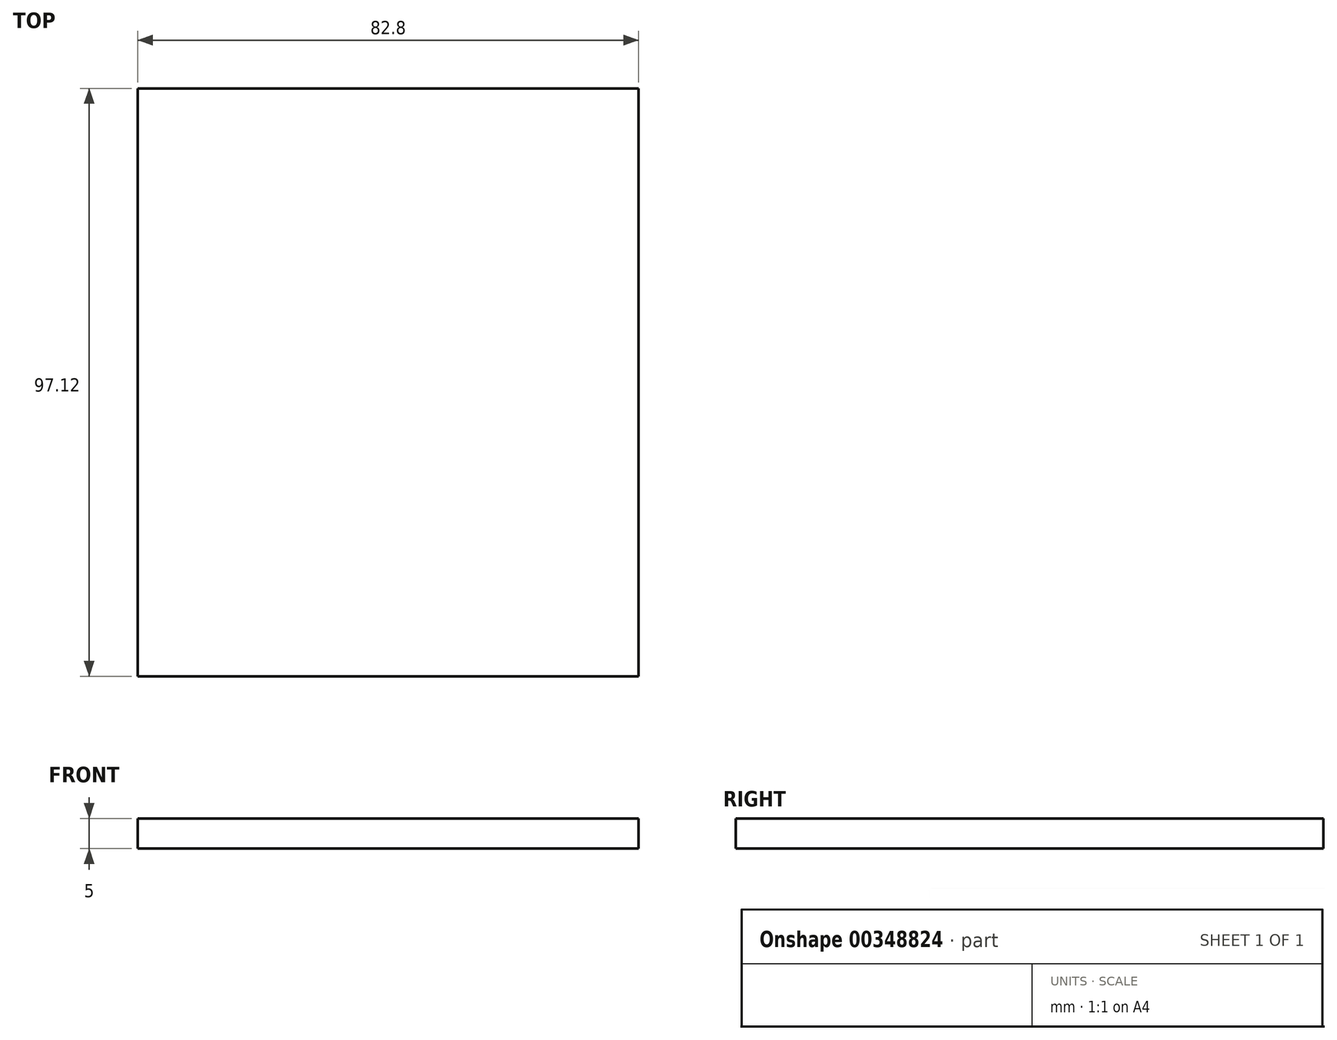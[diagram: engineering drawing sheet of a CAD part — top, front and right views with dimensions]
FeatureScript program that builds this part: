
annotation { "Feature Type Name" : "Feature", "Feature Type Description" : "" }
export const myFeature = defineFeature(function(context is Context, id is Id, definition is map)
    precondition{}
    {
        {
            var Q0;
            Q0=qCreatedBy(makeId("Top.planeOp"),FACE);
            var sketch = newSketch(context, id + "F0", { "sketchPlane" : qUnion([Q0])});
            skLineSegment(sketch, "E0.bottom", {"start": v(-41.4, 48.56) * mm, "end": v(41.4, 48.56) * mm});
            skLineSegment(sketch, "E0.left", {"start": v(-41.4, 48.56) * mm, "end": v(-41.4, -48.56) * mm});
            skLineSegment(sketch, "E0.right", {"start": v(41.4, 48.56) * mm, "end": v(41.4, -48.56) * mm});
            skLineSegment(sketch, "E1", {"start": v(-41.4, -48.56) * mm, "end": v(41.4, -48.56) * mm});
            skSolve(sketch);
        }
        {
            var Q0;
            Q0=makeQuery(id+"F0.imprint","IMPRINT",FACE,{"disambiguationData":[TD([[makeQuery(id+"F0.imprint","IMPRINT",EDGE,{"derivedFrom":sQuery(id+"F0.wireOp",EDGE,"E0.bottom")}),-1.0]])]});
            extrude(context, id + "F1", {"entities" : qUnion([Q0]), "depth" : 5 * mm});
        }
    });
